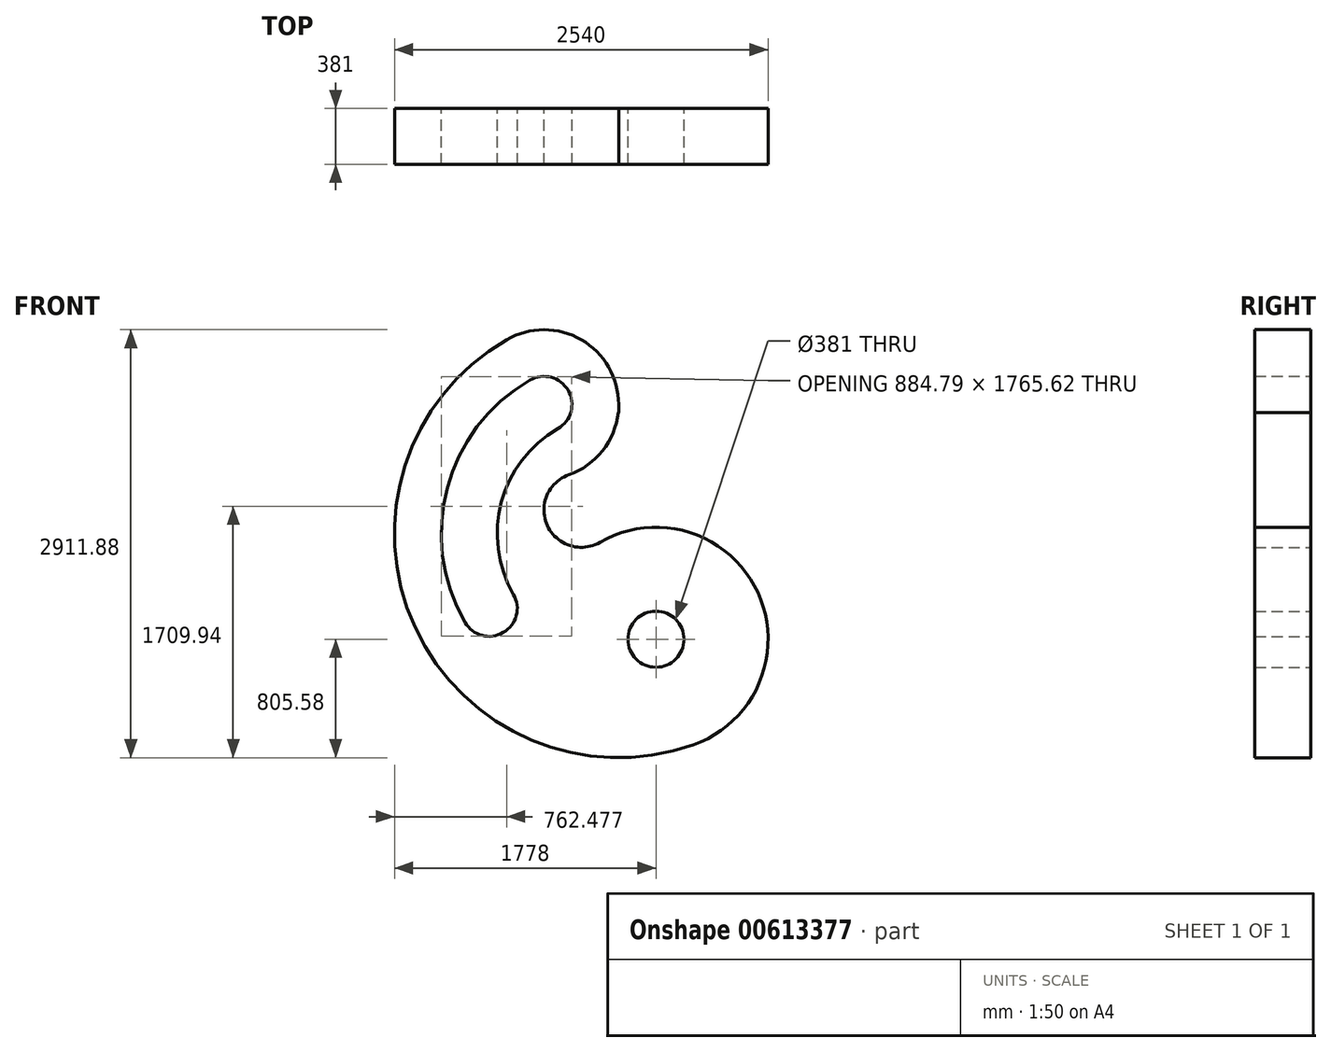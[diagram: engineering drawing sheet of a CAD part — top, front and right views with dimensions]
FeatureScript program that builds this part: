
annotation { "Feature Type Name" : "Feature", "Feature Type Description" : "" }
export const myFeature = defineFeature(function(context is Context, id is Id, definition is map)
    precondition{}
    {
        {
            var Q0;
            Q0=qCreatedBy(makeId("Front.planeOp"),FACE);
            var sketch = newSketch(context, id + "F0", { "sketchPlane" : qUnion([Q0])});
            skArc(sketch, "E0", {"start": v(0, 1016) * mm, "mid": v(-9.26, 1015.96) * mm, "end": v(-18.53, 1015.83) * mm});
            skArc(sketch, "E1", {"start": v(-762, 1319.82) * mm, "mid": v(-1384.17, -637.69) * mm, "end": v(508, -1436.84) * mm});
            skArc(sketch, "E2", {"start": v(-603.25, 1044.86) * mm, "mid": v(-1165.39, 312.27) * mm, "end": v(-1044.86, -603.25) * mm});
            skArc(sketch, "E3", {"start": v(0, 825.5) * mm, "mid": v(-1.46, 825.5) * mm, "end": v(-2.92, 825.5) * mm});
            skArc(sketch, "E4", {"start": v(-412.75, 714.9) * mm, "mid": v(-343.02, 975.13) * mm, "end": v(-603.25, 1044.86) * mm});
            skArc(sketch, "E5", {"start": v(-338.67, 400.93) * mm, "mid": v(-46.6, 1092.45) * mm, "end": v(-762, 1319.82) * mm});
            skArc(sketch, "E6", {"start": v(-1044.86, -603.25) * mm, "mid": v(-784.63, -672.98) * mm, "end": v(-714.9, -412.75) * mm});
            skArc(sketch, "E7.trimOffspring", {"start": v(-412.75, 714.9) * mm, "mid": v(-797.37, 213.66) * mm, "end": v(-714.9, -412.75) * mm});
            skArc(sketch, "E8", {"start": v(-338.67, 400.93) * mm, "mid": v(-484.7, 55.18) * mm, "end": v(-127, -58.5) * mm});
            skCircle(sketch, "E9", {"center": v(254, -718.42) * mm, "radius": 190.5 * mm});
            skArc(sketch, "E10", {"start": v(508, -1436.84) * mm, "mid": v(946.09, -399.58) * mm, "end": v(-127, -58.5) * mm});
            skLineSegment(sketch, "E11.trimOffspring", {"start": v(0, 825.5) * mm, "end": v(0, 879.88) * mm});
            skPoint(sketch, "E12.start.orphan", {"position": v(0, -2927.22) * mm});
            skSolve(sketch);
        }
        {
            var Q0;
            Q0 = qSketchRegion(id + "F0", true);
            extrude(context, id + "F1", {"entities" : qUnion([Q0]), "depth" : 381 * mm, "offsetDistance" : 25.4 * mm});
        }
    });
